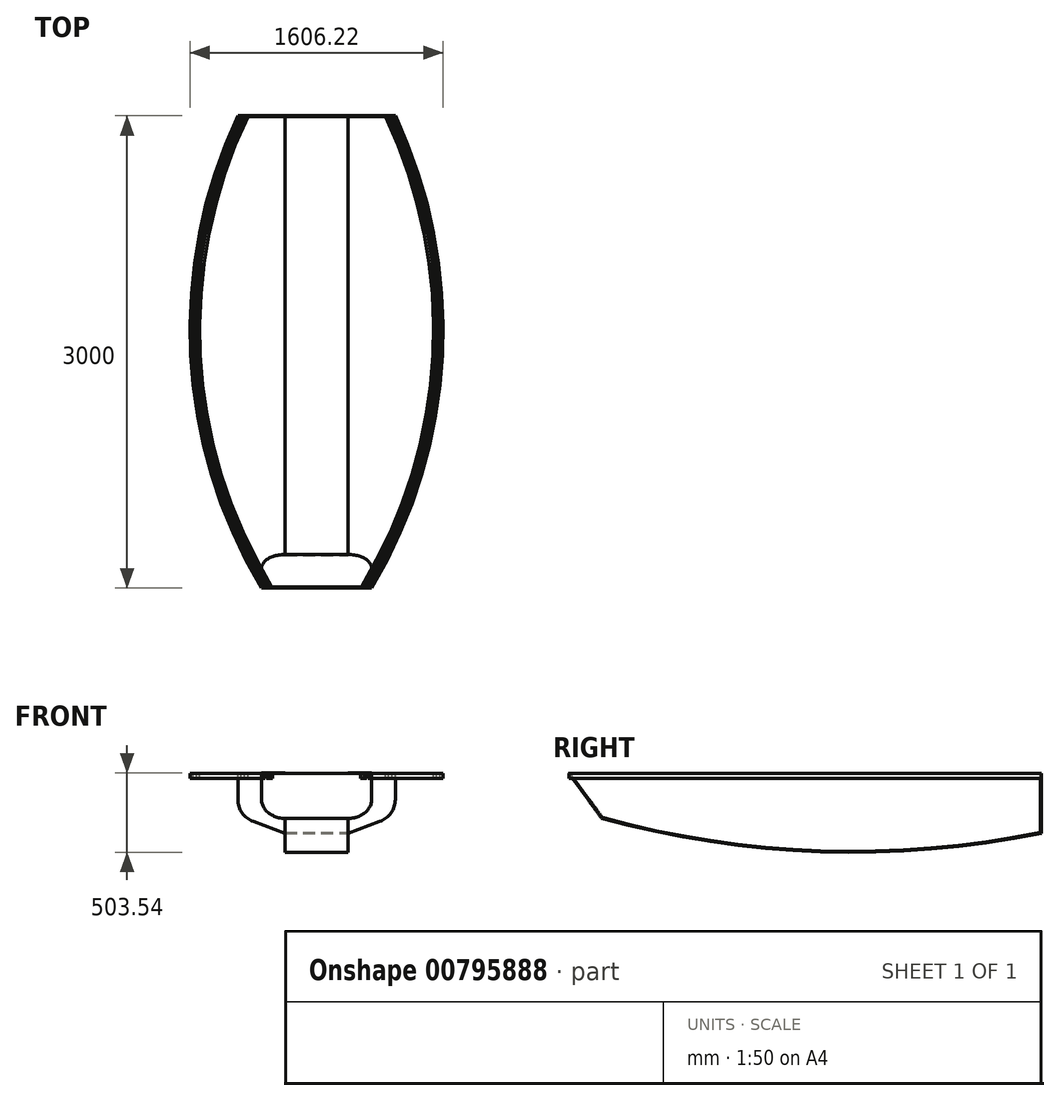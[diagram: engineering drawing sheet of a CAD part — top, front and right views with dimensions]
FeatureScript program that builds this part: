
annotation { "Feature Type Name" : "Feature", "Feature Type Description" : "" }
export const myFeature = defineFeature(function(context is Context, id is Id, definition is map)
    precondition{}
    {
        {
            var Q0;
            Q0=qCreatedBy(makeId("Right.planeOp"),FACE);
            var sketch = newSketch(context, id + "F0", { "sketchPlane" : qUnion([Q0])});
            skLineSegment(sketch, "E0.bottom", {"start": v(0, 0) * mm, "end": v(-3000, 0) * mm});
            skLineSegment(sketch, "E0.top", {"start": v(0, 500) * mm, "end": v(-3000, 500) * mm});
            skLineSegment(sketch, "E0.left", {"start": v(0, 0) * mm, "end": v(0, 500) * mm});
            skLineSegment(sketch, "E0.right", {"start": v(-3000, 0) * mm, "end": v(-3000, 500) * mm});
            skSolve(sketch);
        }
        {
            var Q0;
            Q0=qSketchRegion(id+"F0",true);
            extrude(context, id + "F1", {"entities" : qUnion([Q0]), "depth" : 200 * mm, "offsetDistance" : 25 * mm, "hasSecondDirection" : true, "secondDirectionOppositeDirection" : true, "secondDirectionDepth" : 200 * mm});
        }
        {
            var Q0;
            Q0=makeQuery(id+"F1.opExtrude","CAP_FACE",FACE,{"disambiguationData":[OSD([sQuery(id+"F0.wireOp",EDGE,"E0.bottom"),sQuery(id+"F0.wireOp",EDGE,"E0.top"),sQuery(id+"F0.wireOp",EDGE,"E0.left"),sQuery(id+"F0.wireOp",EDGE,"E0.right")])],"isStart":false});
            var sketch = newSketch(context, id + "F2", { "sketchPlane" : qUnion([Q0])});
            skLineSegment(sketch, "E1.0", {"start": v(0, 0) * mm, "end": v(-3000, 0) * mm});
            skLineSegment(sketch, "E2.0", {"start": v(0, 0) * mm, "end": v(0, 121.22) * mm});
            skArc(sketch, "E3", {"start": v(-2792.04, 215.07) * mm, "mid": v(-1401.56, 3.39) * mm, "end": v(0, 121.22) * mm});
            skPoint(sketch, "E4.orphan", {"position": v(0, 500) * mm});
            skPoint(sketch, "E5.orphan", {"position": v(-2979.63, 270) * mm});
            skPoint(sketch, "E6.start.orphan", {"position": v(-3000, 500) * mm});
            skLineSegment(sketch, "E7", {"start": v(-3000, 500) * mm, "end": v(-3000, 0) * mm});
            skLineSegment(sketch, "E8", {"start": v(-2792.04, 215.07) * mm, "end": v(-3000, 500) * mm});
            skSolve(sketch);
        }
        {
            var Q0;
            Q0=qSketchRegion(id+"F2",true);
            extrude(context, id + "F3", {"entities" : qUnion([Q0]), "operationType" : NewBodyOperationType.REMOVE, "endBound" : BoundingType.THROUGH_ALL, "oppositeDirection" : true, "depth" : 25 * mm, "offsetDistance" : 25 * mm});
        }
        {
            var Q0;
            Q0=makeQuery(id+"F1.opExtrude","CAP_FACE",FACE,{"disambiguationData":[OSD([sQuery(id+"F0.wireOp",EDGE,"E0.bottom"),sQuery(id+"F0.wireOp",EDGE,"E0.top"),sQuery(id+"F0.wireOp",EDGE,"E0.left"),sQuery(id+"F0.wireOp",EDGE,"E0.right")])],"isStart":false});
            var sketch = newSketch(context, id + "F4", { "sketchPlane" : qUnion([Q0])});
            skArc(sketch, "E9.0", {"start": v(-2788.42, 220.3) * mm, "mid": v(-1402.76, 9.43) * mm, "end": v(-6, 126.13) * mm});
            skLineSegment(sketch, "E10.0", {"start": v(-6, 126.13) * mm, "end": v(-6, 500) * mm});
            skLineSegment(sketch, "E11.0", {"start": v(-2788.42, 220.3) * mm, "end": v(-2992.57, 500) * mm});
            skLineSegment(sketch, "E12.0", {"start": v(-6, 500) * mm, "end": v(-2992.57, 500) * mm});
            skPoint(sketch, "E13.orphan", {"position": v(0, 500) * mm});
            skPoint(sketch, "E14.orphan", {"position": v(-3000, 500) * mm});
            skSolve(sketch);
        }
        {
            var Q0;
            Q0=qSketchRegion(id+"F4",true);
            extrude(context, id + "F5", {"entities" : qUnion([Q0]), "operationType" : NewBodyOperationType.REMOVE, "endBound" : BoundingType.THROUGH_ALL, "oppositeDirection" : true, "depth" : 25 * mm, "offsetDistance" : 25 * mm});
        }
        {
            var Q0;
            Q0=qCreatedBy(makeId("Front.planeOp"),FACE);
            cPlane(context, id + "F6", {"entities" : qUnion([Q0]), "cplaneType" : CPlaneType.OFFSET, "offset" : 200 * mm, "width" : 150 * mm, "height" : 150 * mm});
        }
        {
            var Q0;
            Q0=qCreatedBy(id+"F6.planeOp",FACE);
            cPlane(context, id + "F7", {"entities" : qUnion([Q0]), "cplaneType" : CPlaneType.OFFSET, "offset" : 200 * mm, "width" : 150 * mm, "height" : 150 * mm});
        }
        {
            var Q0;
            Q0=qCreatedBy(id+"F7.planeOp",FACE);
            cPlane(context, id + "F8", {"entities" : qUnion([Q0]), "cplaneType" : CPlaneType.OFFSET, "offset" : 200 * mm, "width" : 150 * mm, "height" : 150 * mm});
        }
        {
            var Q0;
            Q0=qCreatedBy(id+"F8.planeOp",FACE);
            cPlane(context, id + "F9", {"entities" : qUnion([Q0]), "cplaneType" : CPlaneType.OFFSET, "offset" : 200 * mm, "width" : 150 * mm, "height" : 150 * mm});
        }
        {
            var Q0;
            Q0=qCreatedBy(id+"F9.planeOp",FACE);
            cPlane(context, id + "F10", {"entities" : qUnion([Q0]), "cplaneType" : CPlaneType.OFFSET, "offset" : 200 * mm, "width" : 150 * mm, "height" : 150 * mm});
        }
        {
            var Q0;
            Q0=qCreatedBy(id+"F10.planeOp",FACE);
            cPlane(context, id + "F11", {"entities" : qUnion([Q0]), "cplaneType" : CPlaneType.OFFSET, "offset" : 200 * mm, "width" : 150 * mm, "height" : 150 * mm});
        }
        {
            var Q0;
            Q0=qCreatedBy(id+"F11.planeOp",FACE);
            cPlane(context, id + "F12", {"entities" : qUnion([Q0]), "cplaneType" : CPlaneType.OFFSET, "offset" : 200 * mm, "width" : 150 * mm, "height" : 150 * mm});
        }
        {
            var Q0;
            Q0=qCreatedBy(id+"F12.planeOp",FACE);
            cPlane(context, id + "F13", {"entities" : qUnion([Q0]), "cplaneType" : CPlaneType.OFFSET, "offset" : 200 * mm, "width" : 150 * mm, "height" : 150 * mm});
        }
        {
            var Q0;
            Q0=qCreatedBy(id+"F13.planeOp",FACE);
            cPlane(context, id + "F14", {"entities" : qUnion([Q0]), "cplaneType" : CPlaneType.OFFSET, "offset" : 200 * mm, "width" : 150 * mm, "height" : 150 * mm});
        }
        {
            var Q0;
            Q0=qCreatedBy(id+"F14.planeOp",FACE);
            cPlane(context, id + "F15", {"entities" : qUnion([Q0]), "cplaneType" : CPlaneType.OFFSET, "offset" : 200 * mm, "width" : 150 * mm, "height" : 150 * mm});
        }
        {
            var Q0;
            Q0=qCreatedBy(id+"F15.planeOp",FACE);
            cPlane(context, id + "F16", {"entities" : qUnion([Q0]), "cplaneType" : CPlaneType.OFFSET, "offset" : 200 * mm, "width" : 150 * mm, "height" : 150 * mm});
        }
        {
            var Q0;
            Q0=qCreatedBy(id+"F16.planeOp",FACE);
            cPlane(context, id + "F17", {"entities" : qUnion([Q0]), "cplaneType" : CPlaneType.OFFSET, "offset" : 200 * mm, "width" : 150 * mm, "height" : 150 * mm});
        }
        {
            var Q0;
            Q0=qCreatedBy(id+"F17.planeOp",FACE);
            cPlane(context, id + "F18", {"entities" : qUnion([Q0]), "cplaneType" : CPlaneType.OFFSET, "offset" : 200 * mm, "width" : 150 * mm, "height" : 150 * mm});
        }
        {
            var Q0;
            Q0=qCreatedBy(id+"F18.planeOp",FACE);
            cPlane(context, id + "F19", {"entities" : qUnion([Q0]), "cplaneType" : CPlaneType.OFFSET, "offset" : 200 * mm, "width" : 150 * mm, "height" : 150 * mm});
        }
        {
            var Q0;
            Q0=qCreatedBy(id+"F19.planeOp",FACE);
            cPlane(context, id + "F20", {"entities" : qUnion([Q0]), "cplaneType" : CPlaneType.OFFSET, "offset" : 200 * mm, "width" : 150 * mm, "height" : 150 * mm});
        }
        {
            var Q0;
            Q0=qCreatedBy(id+"F20.planeOp",FACE);
            cPlane(context, id + "F21", {"entities" : qUnion([Q0]), "cplaneType" : CPlaneType.OFFSET, "offset" : 200 * mm, "width" : 150 * mm, "height" : 150 * mm});
        }
        {
            var Q0;
            Q0=qCreatedBy(id+"F21.planeOp",FACE);
            cPlane(context, id + "F22", {"entities" : qUnion([Q0]), "cplaneType" : CPlaneType.OFFSET, "offset" : 200 * mm, "width" : 150 * mm, "height" : 150 * mm});
        }
        {
            var Q0;
            Q0=qCreatedBy(id+"F22.planeOp",FACE);
            cPlane(context, id + "F23", {"entities" : qUnion([Q0]), "cplaneType" : CPlaneType.OFFSET, "offset" : 200 * mm, "width" : 150 * mm, "height" : 150 * mm});
        }
        {
            var Q0;
            Q0=qCreatedBy(makeId("Top.planeOp"),FACE);
            cPlane(context, id + "F24", {"entities" : qUnion([Q0]), "cplaneType" : CPlaneType.OFFSET, "offset" : 500 * mm, "width" : 150 * mm, "height" : 150 * mm});
        }
        {
            var Q0;
            Q0=makeQuery(id+"F3.boolean.opBoolean","COPY",FACE,{"derivedFrom":makeQuery(id+"F3.opExtrude","SWEPT_FACE",FACE,{"disambiguationData":[OSD([sQuery(id+"F2.wireOp",EDGE,"E8")])]})});
            var sketch = newSketch(context, id + "F25", { "sketchPlane" : qUnion([Q0])});
            skLineSegment(sketch, "E15.0.3", {"start": v(200, 1819.75) * mm, "end": v(-200, 1819.75) * mm});
            skLineSegment(sketch, "E16.0", {"start": v(-200, 1819.75) * mm, "end": v(-200, 2172.5) * mm});
            skLineSegment(sketch, "E17", {"start": v(-200, 2172.5) * mm, "end": v(-350, 2172.5) * mm});
            skPoint(sketch, "E15.0.1.end.orphan", {"position": v(200, 97.92) * mm});
            skPoint(sketch, "E15.0.1.start.orphan", {"position": v(-200, 97.92) * mm});
            skArc(sketch, "E18", {"start": v(-200, 1819.75) * mm, "mid": v(-306.07, 1863.69) * mm, "end": v(-350, 1969.75) * mm});
            skLineSegment(sketch, "E19", {"start": v(-200, 1969.75) * mm, "end": v(-440.1, 1969.75) * mm, "construction": true});
            skLineSegment(sketch, "E20", {"start": v(-350, 1969.75) * mm, "end": v(-350, 2172.5) * mm});
            skSolve(sketch);
        }
        {
            var Q0;
            Q0=qSketchRegion(id+"F25",true);
            extrude(context, id + "F26", {"entities" : qUnion([Q0]), "oppositeDirection" : true, "depth" : 6 * mm, "offsetDistance" : 25 * mm});
        }
        {
            var Q0;
            Q0=makeQuery(id+"F26.opExtrude","SWEPT_BODY",BODY,{"disambiguationData":[OSD([sQuery(id+"F25.wireOp",EDGE,"E16.0"),sQuery(id+"F25.wireOp",EDGE,"E17"),sQuery(id+"F25.wireOp",EDGE,"E18"),sQuery(id+"F25.wireOp",EDGE,"E20")])]});
            var Q1;
            Q1=qCreatedBy(makeId("Right.planeOp"),FACE);
            mirror(context, id + "F27", {"operationType" : NewBodyOperationType.ADD, "entities" : qUnion([Q0]), "mirrorPlane" : qUnion([Q1])});
        }
        {
            var Q0;
            Q0=qCreatedBy(id+"F24.planeOp",FACE);
            var sketch = newSketch(context, id + "F28", { "sketchPlane" : qUnion([Q0])});
            skLineSegment(sketch, "E21", {"start": v(-433.58, 0) * mm, "end": v(-455.75, 0) * mm});
            skLineSegment(sketch, "E22", {"start": v(0, 0) * mm, "end": v(0, -4123.04) * mm, "construction": true});
            skLineSegment(sketch, "E23.0", {"start": v(-200, -3000) * mm, "end": v(-326.44, -3000) * mm, "construction": true});
            skLineSegment(sketch, "E24", {"start": v(0, -1500) * mm, "end": v(-800, -1500) * mm, "construction": true});
            skArc(sketch, "E25", {"start": v(-500, 0) * mm, "mid": v(-799.12, -1518.7) * mm, "end": v(-350, -3000) * mm});
            skArc(sketch, "E26.0", {"start": v(-477.9, 0) * mm, "mid": v(-720.56, -731.55) * mm, "end": v(-779.98, -1500) * mm});
            skArc(sketch, "E27.0", {"start": v(-455.75, 0) * mm, "mid": v(-759.04, -1519.29) * mm, "end": v(-303.3, -3000) * mm});
            skArc(sketch, "E28.0", {"start": v(-433.58, 0) * mm, "mid": v(-739, -1519.59) * mm, "end": v(-279.86, -3000) * mm});
            skLineSegment(sketch, "E29", {"start": v(-279.86, -3000) * mm, "end": v(-303.3, -3000) * mm});
            skLineSegment(sketch, "E30.trimOffspring", {"start": v(-477.9, 0) * mm, "end": v(-500, 0) * mm});
            skLineSegment(sketch, "E31", {"start": v(-350, -3000) * mm, "end": v(-326.44, -3000) * mm});
            skArc(sketch, "E32.0", {"start": v(-779.98, -1500) * mm, "mid": v(-647.22, -2278.38) * mm, "end": v(-326.67, -3000) * mm});
            skLineSegment(sketch, "E33.trimOffspring", {"start": v(-326.67, -3000) * mm, "end": v(-350, -3000) * mm, "construction": true});
            skSolve(sketch);
        }
        {
            var Q0;
            Q0=qSketchRegion(id+"F28",true);
            extrude(context, id + "F29", {"entities" : qUnion([Q0]), "oppositeDirection" : true, "depth" : 30 * mm, "offsetDistance" : 25 * mm});
        }
        {
            var Q0;
            Q0=makeQuery(id+"F29.opExtrude","SWEPT_BODY",BODY,{"disambiguationData":[OSD([sQuery(id+"F28.wireOp",EDGE,"E25"),sQuery(id+"F28.wireOp",EDGE,"E26.0"),sQuery(id+"F28.wireOp",EDGE,"JQv3v1hN-lLp6-lVGY-2l0k-aHUHcDUw9ejT"),sQuery(id+"F28.wireOp",EDGE,"E30.trimOffspring")])]});
            var Q1;
            Q1=makeQuery(id+"F29.opExtrude","SWEPT_BODY",BODY,{"disambiguationData":[OSD([sQuery(id+"F28.wireOp",EDGE,"E21"),sQuery(id+"F28.wireOp",EDGE,"E27.0"),sQuery(id+"F28.wireOp",EDGE,"E28.0"),sQuery(id+"F28.wireOp",EDGE,"E29")])]});
            var Q2;
            Q2=qCreatedBy(makeId("Right.planeOp"),FACE);
            mirror(context, id + "F30", {"operationType" : NewBodyOperationType.ADD, "entities" : qUnion([Q0, Q1]), "mirrorPlane" : qUnion([Q2])});
        }
        {
            var Q0;
            Q0=qCreatedBy(makeId("Front.planeOp"),FACE);
            var sketch = newSketch(context, id + "F31", { "sketchPlane" : qUnion([Q0])});
            skLineSegment(sketch, "E34.0", {"start": v(200, 121.22) * mm, "end": v(200, 500) * mm});
            skLineSegment(sketch, "E35.0", {"start": v(-200, 121.22) * mm, "end": v(200, 121.22) * mm, "construction": true});
            skLineSegment(sketch, "E36.0", {"start": v(500, 470) * mm, "end": v(500, 500) * mm});
            skLineSegment(sketch, "E37", {"start": v(500, 470) * mm, "end": v(500, 335.45) * mm});
            skLineSegment(sketch, "E38", {"start": v(500, 335.45) * mm, "end": v(350, 335.45) * mm, "construction": true});
            skArc(sketch, "E39", {"start": v(401.3, 194.5) * mm, "mid": v(472.87, 249.41) * mm, "end": v(500, 335.45) * mm});
            skLineSegment(sketch, "E40", {"start": v(200, 121.22) * mm, "end": v(401.3, 194.5) * mm});
            skLineSegment(sketch, "E41", {"start": v(500, 500) * mm, "end": v(200, 500) * mm});
            skSolve(sketch);
        }
        {
            var Q0;
            Q0=qSketchRegion(id+"F31",true);
            extrude(context, id + "F32", {"entities" : qUnion([Q0]), "depth" : 6 * mm, "offsetDistance" : 25 * mm});
        }
        {
            var Q0;
            Q0=makeQuery(id+"F32.opExtrude","SWEPT_BODY",BODY,{"disambiguationData":[OSD([sQuery(id+"F31.wireOp",EDGE,"E34.0"),sQuery(id+"F31.wireOp",EDGE,"E36.0"),sQuery(id+"F31.wireOp",EDGE,"E37"),sQuery(id+"F31.wireOp",EDGE,"E39"),sQuery(id+"F31.wireOp",EDGE,"E40"),sQuery(id+"F31.wireOp",EDGE,"E41")])]});
            var Q1;
            Q1=qCreatedBy(makeId("Right.planeOp"),FACE);
            mirror(context, id + "F33", {"operationType" : NewBodyOperationType.ADD, "entities" : qUnion([Q0]), "mirrorPlane" : qUnion([Q1])});
        }
        {
            var Q0;
            Q0=qCreatedBy(id+"F15.planeOp",FACE);
            var sketch = newSketch(context, id + "F34", { "sketchPlane" : qUnion([Q0])});
            skLineSegment(sketch, "E42", {"start": v(-100, 6) * mm, "end": v(-200, 6) * mm});
            skLineSegment(sketch, "E43", {"start": v(-100, 6) * mm, "end": v(-100, 26) * mm});
            skLineSegment(sketch, "E44.0", {"start": v(-100, 26) * mm, "end": v(-200, 26) * mm});
            skLineSegment(sketch, "E45", {"start": v(-200, 6) * mm, "end": v(-200, 156) * mm, "construction": true});
            skLineSegment(sketch, "E46", {"start": v(-200, 156) * mm, "end": v(-282.27, -70.04) * mm, "construction": true});
            skArc(sketch, "E47", {"start": v(-251.3, 15.05) * mm, "mid": v(-226.05, 8.28) * mm, "end": v(-200, 6) * mm});
            skArc(sketch, "E48.0", {"start": v(-244.46, 33.84) * mm, "mid": v(-222.57, 27.97) * mm, "end": v(-200, 26) * mm});
            skLineSegment(sketch, "E49", {"start": v(-803.1, 470) * mm, "end": v(-803.1, 500) * mm});
            skLineSegment(sketch, "E50", {"start": v(-803.1, 470) * mm, "end": v(-803.1, 320.92) * mm});
            skLineSegment(sketch, "E51.0", {"start": v(-783.1, 500) * mm, "end": v(-783.1, 297.72) * mm});
            skLineSegment(sketch, "E52", {"start": v(-803.1, 500) * mm, "end": v(-783.1, 500) * mm});
            skLineSegment(sketch, "E53", {"start": v(-803.1, 320.92) * mm, "end": v(-653.1, 320.92) * mm, "construction": true});
            skArc(sketch, "E54", {"start": v(-803.1, 320.92) * mm, "mid": v(-775.98, 234.88) * mm, "end": v(-704.41, 179.96) * mm});
            skLineSegment(sketch, "E55", {"start": v(-251.3, 15.05) * mm, "end": v(-704.41, 179.96) * mm});
            skArc(sketch, "E56.0", {"start": v(-783.1, 320.92) * mm, "mid": v(-759.6, 246.35) * mm, "end": v(-697.57, 198.76) * mm});
            skLineSegment(sketch, "E57.0", {"start": v(-244.46, 33.84) * mm, "end": v(-697.57, 198.76) * mm});
            skSolve(sketch);
        }
        {
            var Q0;
            Q0=qSketchRegion(id+"F34",true);
            extrude(context, id + "F35", {"entities" : qUnion([Q0]), "depth" : 25 * mm, "offsetDistance" : 25 * mm, "hasSecondDirection" : true, "secondDirectionOppositeDirection" : true, "secondDirectionDepth" : 10 * mm});
        }
        {
            var Q0;
            Q0=makeQuery(id+"F35.opExtrude","SWEPT_BODY",BODY,{"disambiguationData":[OSD([sQuery(id+"F34.wireOp",EDGE,"E42"),sQuery(id+"F34.wireOp",EDGE,"E44.0"),sQuery(id+"F34.wireOp",EDGE,"E47"),sQuery(id+"F34.wireOp",EDGE,"E48.0"),sQuery(id+"F34.wireOp",EDGE,"E49"),sQuery(id+"F34.wireOp",EDGE,"E50"),sQuery(id+"F34.wireOp",EDGE,"E51.0"),sQuery(id+"F34.wireOp",EDGE,"E52"),sQuery(id+"F34.wireOp",EDGE,"E54"),sQuery(id+"F34.wireOp",EDGE,"E55"),sQuery(id+"F34.wireOp",EDGE,"E56.0"),sQuery(id+"F34.wireOp",EDGE,"E57.0"),sQuery(id+"F34.wireOp",EDGE,"E43")])]});
            deleteBodies(context, id + "F36", {"entities" : qUnion([Q0])});
        }
    });
